# Revit family: 28440
name_source: partatom
category: Plumbing Fixtures
units: mm (PartAtom-declared; Revit-internal decimal feet)

## family parameters
Always vertical = Yes
Cut with Voids When Loaded = No
Maintain Annotation Orientation = No
OmniClass Number = 23.45.00.00
OmniClass Title = Sanitary, Laundry, and Cleaning Equipment
Part Type = Normal
Room Calculation Point = No
Round Connector Dimension = Use Diameter
Shared = No
Work Plane-Based = Yes

## types (1)
- 28440-presto
    - Hydraulic supply = 9.00 mm
    -Delivered with = 2 Filter gaskets / - 2 PEX hoses with NF check valves and nuts / - Fixing bracket / - 1 Flange gasket / - 1 Brass clamping nut
    > Standards & approvals = 200-hour neutral salt spray resistant (NSS) in accordance with ISO 9227 / - Brass body in accordance with EN 1982, EN 12164, EN 12156
    > Thermal resistance : = 75.0000 (m²·K)/W
    Default Elevation = 1219 mm
    Description = PRESTO 4000 S single control mixer tap
    Model = 28440
    Recommended pressure = 3.0 bar
    URL = https://www.prestodatashare.com
    brand = LES ROBINETS PRESTO
    flow = 3.0 L/min
    flow time = 15.0 s
    min flow = 1.0 L/min
    min pressure = 1.0 bar
    power = 0 W
    pressure = 5.0 bar
    range = Deck-mounted mixer tap
    ref = 28440 - PRESTO 4000 S single control mixer tap

## geometry (parser evidence)
native form markers: Sweep x2
no freeform markers — native parametric forms only
